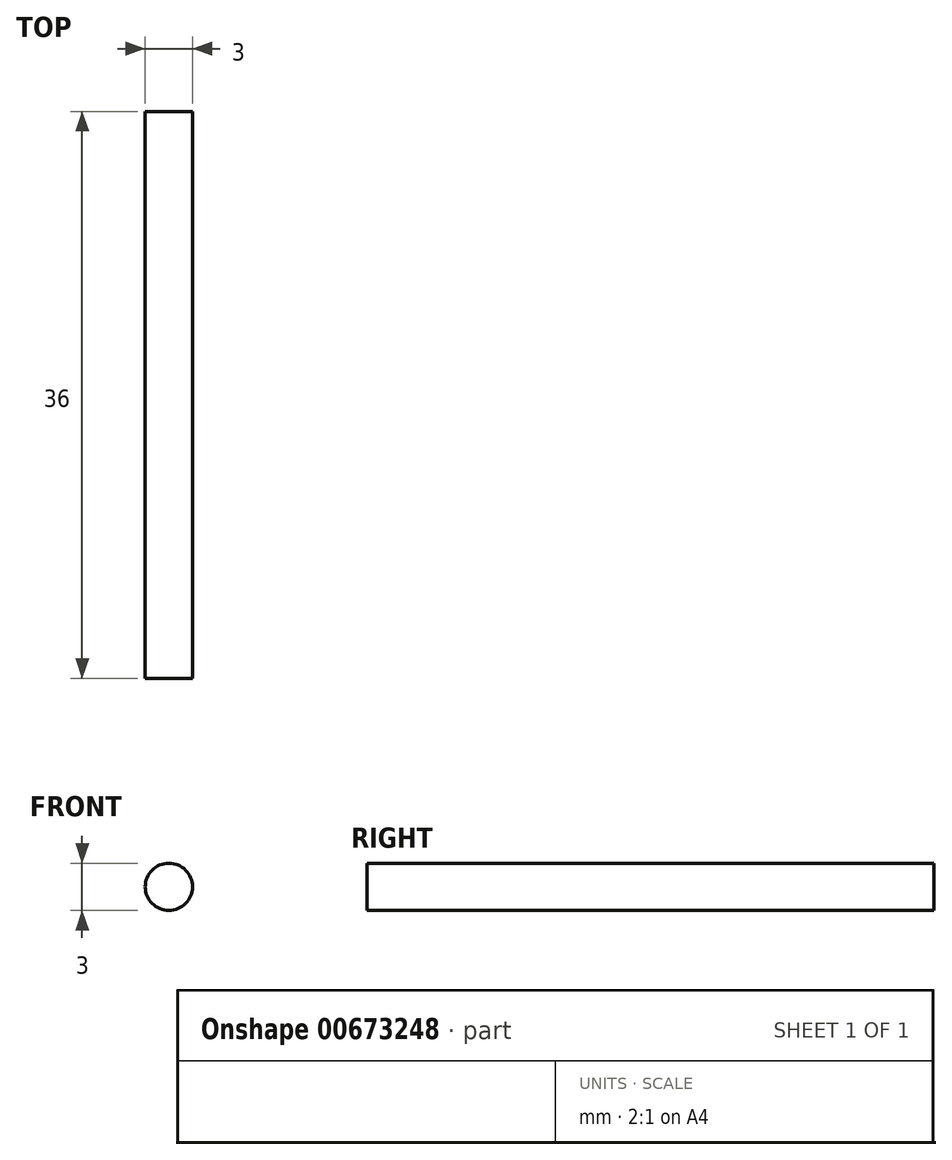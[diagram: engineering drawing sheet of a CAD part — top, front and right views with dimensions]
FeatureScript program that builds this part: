
annotation { "Feature Type Name" : "Feature", "Feature Type Description" : "" }
export const myFeature = defineFeature(function(context is Context, id is Id, definition is map)
    precondition{}
    {
        {
            var Q0;
            Q0=qCreatedBy(makeId("Front.planeOp"),FACE);
            var sketch = newSketch(context, id + "F0", { "sketchPlane" : qUnion([Q0])});
            skCircle(sketch, "E0", {"center": v(0, 0) * mm, "radius": 1.5 * mm});
            skSolve(sketch);
        }
        {
            var Q0;
            Q0 = qSketchRegion(id + "F0", true);
            extrude(context, id + "F1", {"entities" : qUnion([Q0]), "depth" : 36 * mm, "offsetDistance" : 25 * mm});
        }
    });
